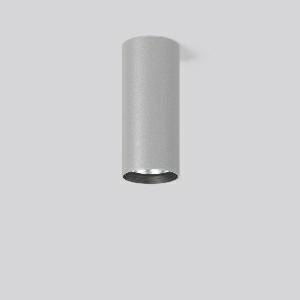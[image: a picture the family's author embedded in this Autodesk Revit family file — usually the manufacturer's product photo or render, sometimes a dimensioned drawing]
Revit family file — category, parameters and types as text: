
# Revit family: heledon_mini_a_931201_004_1_4423
name_source: partatom
category: Lighting Fixtures
units: mm (PartAtom-declared; Revit-internal decimal feet)

## family parameters
Cut with Voids When Loaded = No
Host = Face
Light Source = No
Part Type = Normal
Room Calculation Point = No
Round Connector Dimension = Use Diameter
Shared = No

## types (1)
- HELEDON mini A (1 x LED Modul 940, 2600 lm, 4000)
    Apparent Load = 20 VA
    Approval mark = CE
    CIE Flux Codes = 99 100 100 100 100
    Color Rendering = 92
    Color Temperature = 4000
    Default Elevation = 1800 mm
    Description = Series: HELEDON mini
Cylindrical surface-mounted downlight. Housing: die-cast aluminium, powder-coated. Internal ceiling frame polycarbonate with bayonet mounting. Black plastic ring and recessed LED to prevent glare from the side. Optical assembly with reflector made of MIRO-Silver with 98% total light reflection for outstanding efficiency - can be changed without tools. Best colour rendering index Ra>90. Suitable for Ceiling mounting. Easy installation with a separate ceiling frame with bayonet mounting and plug connection. Driver integrated. Connected via plug-in connector. High quality converter without flickering and stroboscopic effect. The following accessories can be mounted without use of tools: interchangeable lenses, decorative glasses, honeycomb louvre, clear and frosted diffusers, white interchangeable plastic ring. 
Colour: silver
Diameter: 87 mm
Height: 197 mm
Lamp: LED
Socket: without socket
Colour temperature: 4000K
Colour rendering index (CRI): 92
System power: 20 W
Rated luminous flux: 2600 lm
Luminous efficiency: 130 lm/W
Control gear: Regulated power supply
Protection class: I
Type of protection: IP 20
    Height = 197 mm
    Lamp = 1 x LED Modul 940
    Lamp Light Flux = 2600 lm
    Lamp count = 1
    Length = 87 mm
    Lifetime = 50000 h
    Luminous efficacy = 130 lm/W
    Manufacturer = RZB
    ModVariant = No
    Model = 931201.004.1
    Mounting Place = Ceiling
    Mounting Type = Surface mounted
    Number of Poles = 1
    OnlyDefault = Yes
    Power Factor = 1
    Product Name = HELEDON mini A
    Product group = Surface mounted downlights
    ProductGroupID = 302
    Protection Class = Protection class I
    Protection Degree = IP 20
    RLX_Detail_Level = 1
    RLX_Emergency_Light_Flux = 0 lm
    RLX_Emergency_Type = 0
    RLX_Emergency_Type_DB = No
    RlxData = <blob elided: 109445 chars, md5=734d399b>
    Socket = socket
    Standby Power = 0 W
    System Light Flux = 2600 lm
    System Power = 20 W
    Type Comments = Product without accessories
    Type Image = 931188.004.jpg
    URL = http://relux.com
    VarID = ---
    Voltage = 230 V
    Voltage Range = 220-240 V
    Weight = 0.00 kg
    Width = 0 mm  [stored 0 ft]

note: [stored X ft] marks values corroborated as IEEE doubles in the binary element streams (Revit-internal decimal feet)

## geometry (parser evidence)
native form markers: Blend x4, Sweep x9
no freeform markers — native parametric forms only
